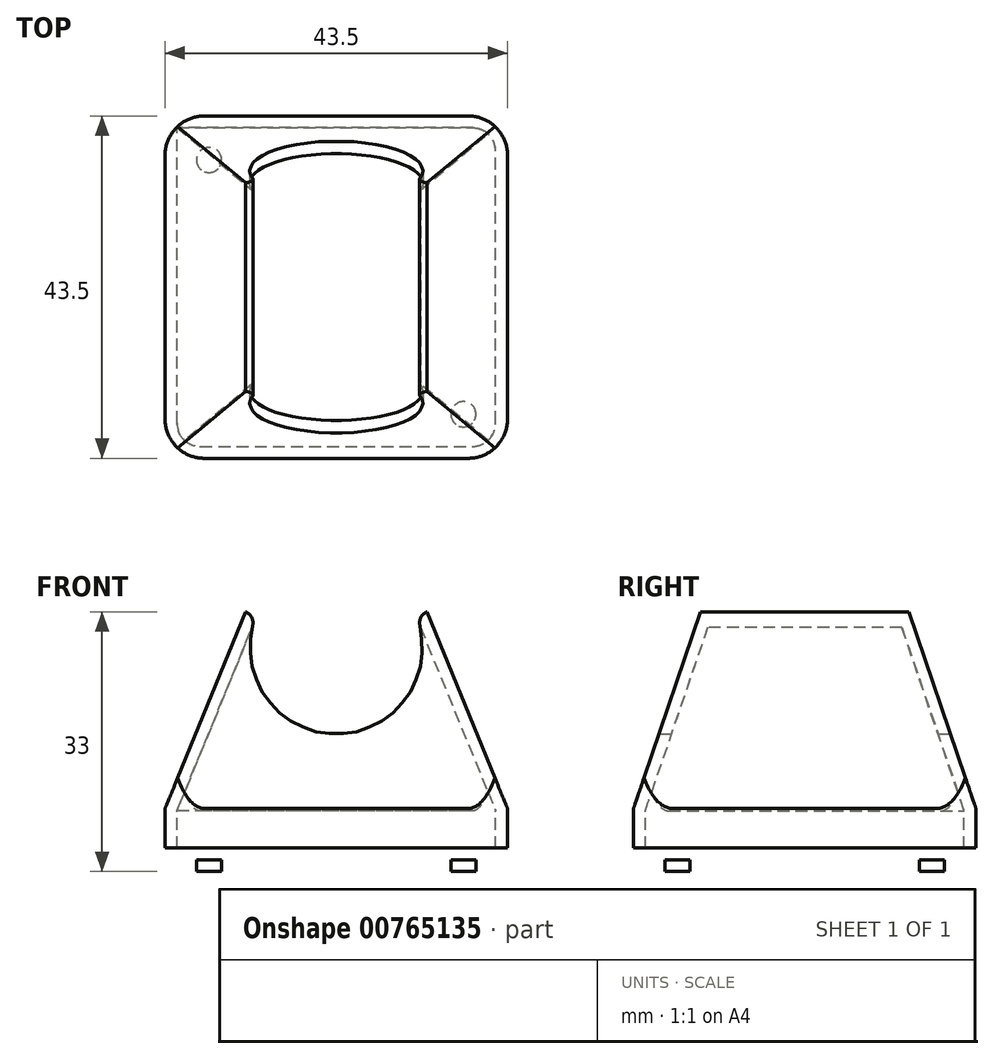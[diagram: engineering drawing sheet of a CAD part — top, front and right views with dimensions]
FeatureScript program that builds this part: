
annotation { "Feature Type Name" : "Feature", "Feature Type Description" : "" }
export const myFeature = defineFeature(function(context is Context, id is Id, definition is map)
    precondition{}
    {
        {
            var Q0;
            Q0=qCreatedBy(makeId("Top.planeOp"),FACE);
            var sketch = newSketch(context, id + "F0", { "sketchPlane" : qUnion([Q0])});
            skLineSegment(sketch, "E0.bottom", {"start": v(-21.75, -21.75) * mm, "end": v(21.75, -21.75) * mm});
            skLineSegment(sketch, "E0.top", {"start": v(-21.75, 21.75) * mm, "end": v(21.75, 21.75) * mm});
            skLineSegment(sketch, "E0.left", {"start": v(-21.75, -21.75) * mm, "end": v(-21.75, 21.75) * mm});
            skLineSegment(sketch, "E0.right", {"start": v(21.75, -21.75) * mm, "end": v(21.75, 21.75) * mm});
            skPoint(sketch, "E0.middle", {"position": v(0, 0) * mm});
            skSolve(sketch);
        }
        {
            var Q0;
            Q0=qCreatedBy(makeId("Top.planeOp"),FACE);
            cPlane(context, id + "F1", {"entities" : qUnion([Q0]), "cplaneType" : CPlaneType.OFFSET, "offset" : 25 * mm, "width" : 150 * mm, "height" : 150 * mm});
        }
        {
            var Q0;
            Q0=qCreatedBy(id+"F1.planeOp",FACE);
            var sketch = newSketch(context, id + "F2", { "sketchPlane" : qUnion([Q0])});
            skLineSegment(sketch, "E1.bottom", {"start": v(-11.5, 13.25) * mm, "end": v(11.5, 13.25) * mm});
            skLineSegment(sketch, "E1.top", {"start": v(-11.5, -13.25) * mm, "end": v(11.5, -13.25) * mm});
            skLineSegment(sketch, "E1.left", {"start": v(-11.5, 13.25) * mm, "end": v(-11.5, -13.25) * mm});
            skLineSegment(sketch, "E1.right", {"start": v(11.5, 13.25) * mm, "end": v(11.5, -13.25) * mm});
            skPoint(sketch, "E1.middle", {"position": v(0, 0) * mm});
            skSolve(sketch);
        }
        {
            var Q0;
            Q0=makeQuery(id+"F0.imprint","IMPRINT",FACE,{"disambiguationData":[TD([[makeQuery(id+"F0.imprint","IMPRINT",EDGE,{"derivedFrom":sQuery(id+"F0.wireOp",EDGE,"E0.bottom")}),1.0]])]});
            var Q1;
            Q1=makeQuery(id+"F2.imprint","IMPRINT",FACE,{"disambiguationData":[TD([[makeQuery(id+"F2.imprint","IMPRINT",EDGE,{"derivedFrom":sQuery(id+"F2.wireOp",EDGE,"E1.bottom")}),-1.0]])]});
            loft(context, id + "F3", {"sheetProfilesArray" : [{ "sheetProfileEntities" : qUnion([Q0]) }, { "sheetProfileEntities" : qUnion([Q1]) }]});
        }
        {
            var Q0;
            Q0=makeQuery(id+"F3.opLoft","CAP_FACE",FACE,{"disambiguationData":[OSD([makeQuery(id+"F0.imprint","IMPRINT",FACE,{"disambiguationData":[TD([[makeQuery(id+"F0.imprint","IMPRINT",EDGE,{"derivedFrom":sQuery(id+"F0.wireOp",EDGE,"E0.bottom")}),1.0]])]})])],"isStart":true});
            extrude(context, id + "F4", {"entities" : qUnion([Q0]), "operationType" : NewBodyOperationType.ADD, "depth" : 8 * mm, "offsetDistance" : 25 * mm});
        }
        {
            var Q0;
            Q0=makeQuery(id+"F3.opLoft","CAP_FACE",FACE,{"disambiguationData":[OSD([makeQuery(id+"F2.imprint","IMPRINT",FACE,{"disambiguationData":[TD([[makeQuery(id+"F2.imprint","IMPRINT",EDGE,{"derivedFrom":sQuery(id+"F2.wireOp",EDGE,"E1.bottom")}),-1.0]])]})])],"isStart":true});
            shell(context, id + "F5", {"entities" : qUnion([Q0]), "thickness" : 1.5 * mm});
        }
        {
            var Q0;
            Q0=makeQuery(id+"F4.opExtrude","CAP_FACE",FACE,{"disambiguationData":[OSD([makeQuery(id+"F0.imprint","IMPRINT",FACE,{"disambiguationData":[TD([[makeQuery(id+"F0.imprint","IMPRINT",EDGE,{"derivedFrom":sQuery(id+"F0.wireOp",EDGE,"E0.bottom")}),1.0]])]})])],"isStart":false});
            var sketch = newSketch(context, id + "F6", { "sketchPlane" : qUnion([Q0])});
            skCircle(sketch, "E2", {"center": v(0, 0) * mm, "radius": 18.75 * mm});
            skLineSegment(sketch, "E3", {"start": v(0, 30.8) * mm, "end": v(0, -38.34) * mm, "construction": true});
            skLineSegment(sketch, "E4", {"start": v(-21.75, 0) * mm, "end": v(21.75, 0) * mm, "construction": true});
            skCircle(sketch, "E5", {"center": v(-16.15, 16.15) * mm, "radius": 1.6 * mm});
            skCircle(sketch, "E6.MirrorC", {"center": v(16.15, 16.15) * mm, "radius": 1.6 * mm});
            skCircle(sketch, "E7.MirrorC", {"center": v(-16.15, -16.15) * mm, "radius": 1.6 * mm});
            skCircle(sketch, "E8.MirrorC", {"center": v(16.15, -16.15) * mm, "radius": 1.6 * mm});
            skSolve(sketch);
        }
        {
            var Q0;
            Q0=makeQuery(id+"F6.imprint","IMPRINT",FACE,{"disambiguationData":[TD([[makeQuery(id+"F6.imprint","IMPRINT",EDGE,{"derivedFrom":sQuery(id+"F6.wireOp",EDGE,"E2")}),1.0]])]});
            var Q1;
            Q1=makeQuery(id+"F6.imprint","IMPRINT",FACE,{"disambiguationData":[TD([[makeQuery(id+"F6.imprint","IMPRINT",EDGE,{"derivedFrom":sQuery(id+"F6.wireOp",EDGE,"E5")}),1.0]])]});
            var Q2;
            Q2=makeQuery(id+"F6.imprint","IMPRINT",FACE,{"disambiguationData":[TD([[makeQuery(id+"F6.imprint","IMPRINT",EDGE,{"derivedFrom":sQuery(id+"F6.wireOp",EDGE,"E6.MirrorC")}),-1.0]])]});
            var Q3;
            Q3=makeQuery(id+"F6.imprint","IMPRINT",FACE,{"disambiguationData":[TD([[makeQuery(id+"F6.imprint","IMPRINT",EDGE,{"derivedFrom":sQuery(id+"F6.wireOp",EDGE,"E8.MirrorC")}),1.0]])]});
            var Q4;
            Q4=makeQuery(id+"F6.imprint","IMPRINT",FACE,{"disambiguationData":[TD([[makeQuery(id+"F6.imprint","IMPRINT",EDGE,{"derivedFrom":sQuery(id+"F6.wireOp",EDGE,"E7.MirrorC")}),-1.0]])]});
            extrude(context, id + "F7", {"entities" : qUnion([Q0, Q1, Q2, Q3, Q4]), "operationType" : NewBodyOperationType.REMOVE, "oppositeDirection" : true, "depth" : 3 * mm, "offsetDistance" : 25 * mm});
        }
        {
            var Q0;
            Q0=makeQuery(id+"F4.opExtrude","SWEPT_FACE",FACE,{"disambiguationData":[OSD([sQuery(id+"F0.wireOp",EDGE,"E0.bottom"),sQuery(id+"F0.wireOp",EDGE,"E0.left"),sQuery(id+"F0.wireOp",EDGE,"E0.right")])]});
            var sketch = newSketch(context, id + "F8", { "sketchPlane" : qUnion([Q0])});
            skLineSegment(sketch, "E9.0", {"start": v(-11.5, 25) * mm, "end": v(11.5, 25) * mm});
            skPoint(sketch, "E10", {"position": v(-10, 25) * mm});
            skPoint(sketch, "E11", {"position": v(10, 25) * mm});
            skCircle(sketch, "E12", {"center": v(0, 20.42) * mm, "radius": 11 * mm});
            skSolve(sketch);
        }
        {
            var Q0;
            {var subQ0=sQuery(id+"F8.wireOp",EDGE,"E12");var subQ1=sQuery(id+"F8.wireOp",EDGE,"E9.0");var subQ2=makeQuery(id+"F8.imprint","INTERSECT",VERTEX,{"disambiguationData":[OD(0.0)],"derivedFrom":[subQ1,subQ0]});Q0=makeQuery(id+"F8.imprint","IMPRINT",FACE,{"disambiguationData":[TD([[makeQuery(id+"F8.imprint","IMPRINT",EDGE,{"disambiguationData":[TD([[subQ2,-1.0]])],"derivedFrom":subQ1}),-1.0]])]});}
            var Q1;
            {var subQ0=sQuery(id+"F8.wireOp",EDGE,"E12");var subQ1=sQuery(id+"F8.wireOp",EDGE,"E9.0");var subQ2=makeQuery(id+"F8.imprint","INTERSECT",VERTEX,{"disambiguationData":[OD(0.0)],"derivedFrom":[subQ1,subQ0]});Q1=makeQuery(id+"F8.imprint","IMPRINT",FACE,{"disambiguationData":[TD([[makeQuery(id+"F8.imprint","IMPRINT",EDGE,{"disambiguationData":[TD([[subQ2,-1.0]])],"derivedFrom":subQ1}),1.0]])]});}
            extrude(context, id + "F9", {"entities" : qUnion([Q0, Q1]), "operationType" : NewBodyOperationType.REMOVE, "oppositeDirection" : true, "depth" : 50 * mm, "offsetDistance" : 25 * mm});
        }
        {
            var Q0;
            {var subQ0=sQuery(id+"F0.wireOp",EDGE,"E0.left");var subQ1=sQuery(id+"F0.wireOp",EDGE,"E0.top");var subQ2=sQuery(id+"F0.wireOp",EDGE,"E0.bottom");Q0=makeQuery(id+"F5.opShell","OFFSET_EDGE",EDGE,{"disambiguationData":[OSD([subQ2,subQ1,subQ0]),TDD([makeQuery(id+"F4.opExtrude","CAP_EDGE",EDGE,{"disambiguationData":[OSD([subQ2,subQ1,subQ0])],"isStart":false})])]});}
            var Q1;
            {var subQ0=sQuery(id+"F0.wireOp",EDGE,"E0.right");var subQ1=sQuery(id+"F0.wireOp",EDGE,"E0.left");var subQ2=sQuery(id+"F0.wireOp",EDGE,"E0.top");Q1=makeQuery(id+"F5.opShell","OFFSET_EDGE",EDGE,{"disambiguationData":[OSD([subQ2,subQ1,subQ0]),TDD([makeQuery(id+"F4.opExtrude","CAP_EDGE",EDGE,{"disambiguationData":[OSD([subQ2,subQ1,subQ0])],"isStart":false})])]});}
            var Q2;
            {var subQ0=sQuery(id+"F0.wireOp",EDGE,"E0.right");var subQ1=sQuery(id+"F0.wireOp",EDGE,"E0.left");var subQ2=sQuery(id+"F0.wireOp",EDGE,"E0.bottom");Q2=makeQuery(id+"F5.opShell","OFFSET_EDGE",EDGE,{"disambiguationData":[OSD([subQ2,subQ1,subQ0]),TDD([makeQuery(id+"F4.opExtrude","CAP_EDGE",EDGE,{"disambiguationData":[OSD([subQ2,subQ1,subQ0])],"isStart":false})])]});}
            var Q3;
            {var subQ0=sQuery(id+"F0.wireOp",EDGE,"E0.right");var subQ1=sQuery(id+"F0.wireOp",EDGE,"E0.top");var subQ2=sQuery(id+"F0.wireOp",EDGE,"E0.bottom");Q3=makeQuery(id+"F5.opShell","OFFSET_EDGE",EDGE,{"disambiguationData":[OSD([subQ2,subQ1,subQ0]),TDD([makeQuery(id+"F4.opExtrude","CAP_EDGE",EDGE,{"disambiguationData":[OSD([subQ2,subQ1,subQ0])],"isStart":false})])]});}
            var Q4;
            Q4=makeQuery(id+"F9.boolean.opBoolean","INTERSECT",EDGE,{"disambiguationData":[OD(1.0)],"derivedFrom":[makeQuery(id+"F3.opLoft","CAP_FACE",FACE,{"disambiguationData":[OSD([makeQuery(id+"F2.imprint","IMPRINT",FACE,{"disambiguationData":[TD([[makeQuery(id+"F2.imprint","IMPRINT",EDGE,{"derivedFrom":sQuery(id+"F2.wireOp",EDGE,"E1.bottom")}),-1.0]])]})])],"isStart":true}),makeQuery(id+"F9.opExtrude","SWEPT_FACE",FACE,{"disambiguationData":[OSD([sQuery(id+"F8.wireOp",EDGE,"E12")])]})]});
            var Q5;
            Q5=makeQuery(id+"F9.boolean.opBoolean","INTERSECT",EDGE,{"disambiguationData":[OD(0.0)],"derivedFrom":[makeQuery(id+"F3.opLoft","CAP_FACE",FACE,{"disambiguationData":[OSD([makeQuery(id+"F2.imprint","IMPRINT",FACE,{"disambiguationData":[TD([[makeQuery(id+"F2.imprint","IMPRINT",EDGE,{"derivedFrom":sQuery(id+"F2.wireOp",EDGE,"E1.bottom")}),-1.0]])]})])],"isStart":true}),makeQuery(id+"F9.opExtrude","SWEPT_FACE",FACE,{"disambiguationData":[OSD([sQuery(id+"F8.wireOp",EDGE,"E12")])]})]});
            fillet(context, id + "F10", {"entities" : qUnion([Q0, Q1, Q2, Q3, Q4, Q5]), "radius" : 1.5 * mm, "tangentPropagation" : true, "allowEdgeOverflow" : false});
        }
        {
            var Q0;
            Q0=makeQuery(id+"F4.opExtrude","SWEPT_EDGE",EDGE,{"disambiguationData":[OSD([sQuery(id+"F0.wireOp",EDGE,"E0.bottom"),sQuery(id+"F0.wireOp",EDGE,"E0.right")])]});
            var Q1;
            Q1=makeQuery(id+"F4.opExtrude","SWEPT_EDGE",EDGE,{"disambiguationData":[OSD([sQuery(id+"F0.wireOp",EDGE,"E0.top"),sQuery(id+"F0.wireOp",EDGE,"E0.left")])]});
            var Q2;
            Q2=makeQuery(id+"F4.opExtrude","SWEPT_EDGE",EDGE,{"disambiguationData":[OSD([sQuery(id+"F0.wireOp",EDGE,"E0.bottom"),sQuery(id+"F0.wireOp",EDGE,"E0.left")])]});
            var Q3;
            Q3=makeQuery(id+"F4.opExtrude","SWEPT_EDGE",EDGE,{"disambiguationData":[OSD([sQuery(id+"F0.wireOp",EDGE,"E0.top"),sQuery(id+"F0.wireOp",EDGE,"E0.right")])]});
            fillet(context, id + "F11", {"entities" : qUnion([Q0, Q1, Q2, Q3]), "radius" : 5 * mm, "tangentPropagation" : true, "allowEdgeOverflow" : false});
        }
        {
            var Q0;
            Q0=makeQuery(id+"F5.opShell","OFFSET_EDGE",EDGE,{"disambiguationData":[OSD([sQuery(id+"F0.wireOp",EDGE,"E0.bottom"),sQuery(id+"F0.wireOp",EDGE,"E0.left")])]});
            var Q1;
            {var subQ0=sQuery(id+"F0.wireOp",EDGE,"E0.right");var subQ1=sQuery(id+"F0.wireOp",EDGE,"E0.left");var subQ2=sQuery(id+"F0.wireOp",EDGE,"E0.top");var subQ3=sQuery(id+"F0.wireOp",EDGE,"E0.bottom");Q1=makeQuery(id+"F10.opFillet","BLEND_EDGE",EDGE,{"blendedFrom":[makeQuery(id+"F5.opShell","OFFSET_EDGE",EDGE,{"disambiguationData":[OSD([subQ3,subQ2,subQ1]),TDD([makeQuery(id+"F4.opExtrude","CAP_EDGE",EDGE,{"disambiguationData":[OSD([subQ3,subQ2,subQ1])],"isStart":false})])]}),makeQuery(id+"F5.opShell","OFFSET_EDGE",EDGE,{"disambiguationData":[OSD([subQ2,subQ1,subQ0]),TDD([makeQuery(id+"F4.opExtrude","CAP_EDGE",EDGE,{"disambiguationData":[OSD([subQ2,subQ1,subQ0])],"isStart":false})])]})],"blendedInto":[]});}
            var Q2;
            Q2=makeQuery(id+"F5.opShell","OFFSET_EDGE",EDGE,{"disambiguationData":[OSD([sQuery(id+"F0.wireOp",EDGE,"E0.top"),sQuery(id+"F0.wireOp",EDGE,"E0.right")])]});
            var Q3;
            Q3=makeQuery(id+"F5.opShell","OFFSET_EDGE",EDGE,{"disambiguationData":[OSD([sQuery(id+"F0.wireOp",EDGE,"E0.bottom"),sQuery(id+"F0.wireOp",EDGE,"E0.right")])]});
            fillet(context, id + "F12", {"entities" : qUnion([Q0, Q1, Q2, Q3]), "radius" : 3 * mm, "tangentPropagation" : true, "allowEdgeOverflow" : false});
        }
    });
